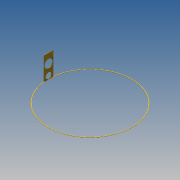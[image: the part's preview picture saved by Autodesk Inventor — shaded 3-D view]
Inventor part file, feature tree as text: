
AUTODESK INVENTOR PART (.ipt)
format: ipt  version: 2014 SP1 (Build 180222100, 222)  size: 110,592 bytes
history: native  units: in
note: dims shown in document units (in); Inventor stores cm internally (conversion verified against a paired STEP export)
features: extrude x4, sketch x4
ambient origin geometry x8: Origin, YZ Plane, XZ Plane, XY Plane, X Axis, Y Axis, Z Axis, Center Point
bodies: Solid1 (feature_tree)
feature tree (8):
  extrude  "Extrusion1"  Depth=0.25in
  extrude  "Extrusion2"  Depth=0.1in
  extrude  "Extrusion3"  Depth=10.0in TaperAngle=0.0deg
  extrude  "Extrusion4"  Depth=0.1in TaperAngle=0.0deg
  sketch  "Sketch1"  dims[d0=36.0in d1=0.25in]
  sketch  "Sketch2"  dims[d2=0.1in d3=0.0in d4=0.1in]
  sketch  "Sketch3"  dims[d5=4.0in d6=10.0in d7=0.0in]
  sketch  "Sketch4"  dims[d8=0.02in d9=0.1in d10=0.0in d11=3.5433in d12=4.1in d13=2.4803in d14=8.6024in d15=0.0in d16=0.0in]
